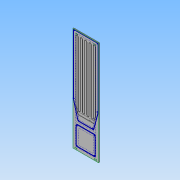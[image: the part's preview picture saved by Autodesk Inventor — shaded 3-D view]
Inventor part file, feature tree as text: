
AUTODESK INVENTOR PART (.ipt)
format: ipt  version: 2013 (Build 170138000, 138)  size: 339,968 bytes
history: native  units: in
note: dims shown in document units (in); Inventor stores cm internally (conversion verified against a paired STEP export)
features: other x13, extrude x3, hole x1, plane x1
ambient origin geometry x8: Origin, YZ Plane, XZ Plane, XY Plane, X Axis, Y Axis, Z Axis, Center Point
bodies: Solid1 (feature_tree)
feature tree (18):
  other  "Blocks"
  extrude  "Stock Extrusion"  Depth=23.8125in
  extrude  "Main rope pocket"  Depth=96.0in
  other  "Side profile reference"
  hole  "Hole1"  [1 undecoded]
  plane  "Work Plane1"
  extrude  "Through Panel Extrusion5"  Depth=58.0in
  other  "Exclaim Point"
  other  "Stock"
  other  "LEDPocket"
  other  "TwoLineColumn"
  other  "TwoLineColumnEnd"
  other  "15mm Neon profile"
  other  "U Bolt hole and bore"
  other  "U-Bolt holes"
  other  "WeatherProof panel"
  other  "15mm Neon profile:1"
  other  "15mm Neon profile:2"
note: 1 required parameter value undecoded (feature->parameter linkage not recoverable at this tier; creation-order binding heuristic only, values carry confidence <= 0.55)
